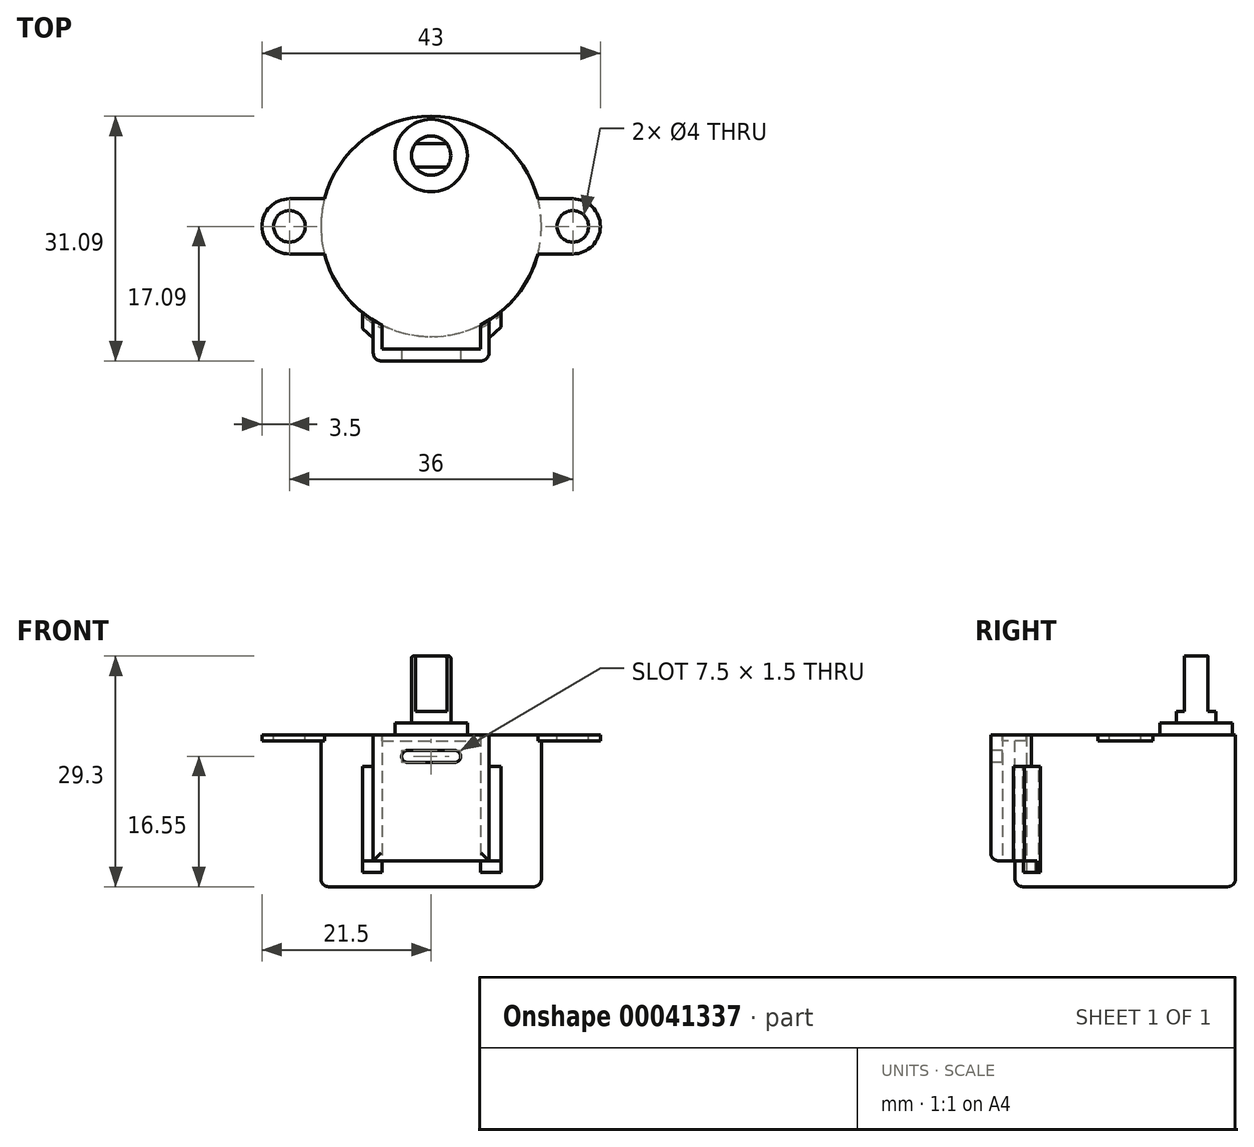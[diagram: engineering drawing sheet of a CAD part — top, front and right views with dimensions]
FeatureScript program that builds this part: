
annotation { "Feature Type Name" : "Feature", "Feature Type Description" : "" }
export const myFeature = defineFeature(function(context is Context, id is Id, definition is map)
    precondition{}
    {
        {
            var Q0;
            Q0=qCreatedBy(makeId("Top.planeOp"),FACE);
            var sketch = newSketch(context, id + "F0", { "sketchPlane" : qUnion([Q0])});
            skCircle(sketch, "E0", {"center": v(0, 0) * mm, "radius": 14 * mm});
            skLineSegment(sketch, "E1", {"start": v(-13.56, 3.5) * mm, "end": v(-18, 3.5) * mm});
            skLineSegment(sketch, "E2", {"start": v(-13.56, -3.5) * mm, "end": v(-18, -3.5) * mm});
            skArc(sketch, "E3", {"start": v(-18, -3.5) * mm, "mid": v(-21.5, 0) * mm, "end": v(-18, 3.5) * mm});
            skCircle(sketch, "E4", {"center": v(-18, 0) * mm, "radius": 2 * mm});
            skLineSegment(sketch, "E5", {"start": v(0, 23.7) * mm, "end": v(0, -18.74) * mm, "construction": true});
            skLineSegment(sketch, "E6.MirrorCS", {"start": v(13.56, -3.5) * mm, "end": v(18, -3.5) * mm});
            skLineSegment(sketch, "E7.MirrorCS", {"start": v(13.56, 3.5) * mm, "end": v(18, 3.5) * mm});
            skArc(sketch, "E8.MirrorCS", {"start": v(18, -3.5) * mm, "mid": v(21.5, 0) * mm, "end": v(18, 3.5) * mm});
            skCircle(sketch, "E9.MirrorC", {"center": v(18, 0) * mm, "radius": 2 * mm});
            skLineSegment(sketch, "E10", {"start": v(-6.25, -12.53) * mm, "end": v(-6.25, -15.6) * mm});
            skLineSegment(sketch, "E11", {"start": v(-6.25, -15.6) * mm, "end": v(6.25, -15.6) * mm});
            skLineSegment(sketch, "E12", {"start": v(6.25, -15.6) * mm, "end": v(6.25, -12.53) * mm});
            skCircle(sketch, "E13", {"center": v(0, 9) * mm, "radius": 4.6 * mm});
            skCircle(sketch, "E14", {"center": v(0, 9) * mm, "radius": 2.5 * mm});
            skLineSegment(sketch, "E15", {"start": v(7.35, -11.92) * mm, "end": v(7.35, -17.1) * mm});
            skLineSegment(sketch, "E16", {"start": v(7.35, -17.1) * mm, "end": v(-7.35, -17.1) * mm});
            skLineSegment(sketch, "E17", {"start": v(-7.35, -17.1) * mm, "end": v(-7.35, -11.92) * mm});
            skLineSegment(sketch, "E18", {"start": v(8.9, -10.8) * mm, "end": v(8.9, -12.8) * mm});
            skLineSegment(sketch, "E19", {"start": v(8.9, -12.8) * mm, "end": v(7.35, -14.21) * mm});
            skLineSegment(sketch, "E20", {"start": v(-8.7, -10.97) * mm, "end": v(-8.7, -12.97) * mm});
            skLineSegment(sketch, "E21", {"start": v(-8.7, -12.97) * mm, "end": v(-7.35, -14.21) * mm});
            skPoint(sketch, "E22", {"position": v(-7.35, -14.5) * mm});
            skArc(sketch, "E23.trimOffspring", {"start": v(-8.7, -11.4) * mm, "mid": v(-5.3, -13.35) * mm, "end": v(-1.5, -14.3) * mm});
            skLineSegment(sketch, "E24", {"start": v(1.5, -14.3) * mm, "end": v(1.5, -13.92) * mm});
            skLineSegment(sketch, "E25", {"start": v(-1.5, -14.3) * mm, "end": v(-1.5, -13.92) * mm});
            skArc(sketch, "E26.trimOffspring", {"start": v(1.5, -14.3) * mm, "mid": v(5.43, -13.3) * mm, "end": v(8.9, -11.22) * mm});
            skLineSegment(sketch, "E27", {"start": v(-2, 10.5) * mm, "end": v(2, 10.5) * mm});
            skLineSegment(sketch, "E28", {"start": v(-2, 7.5) * mm, "end": v(2, 7.5) * mm});
            skSolve(sketch);
        }
        {
            var Q0;
            {var subQ0=sQuery(id+"F0.wireOp",EDGE,"E1");Q0=makeQuery(id+"F0.imprint","IMPRINT",FACE,{"disambiguationData":[TD([[makeQuery(id+"F0.imprint","IMPRINT",EDGE,{"derivedFrom":subQ0}),1.0]])]});}
            var Q1;
            Q1=makeQuery(id+"F0.imprint","IMPRINT",FACE,{"disambiguationData":[TD([[makeQuery(id+"F0.imprint","IMPRINT",EDGE,{"derivedFrom":sQuery(id+"F0.wireOp",EDGE,"E13")}),-1.0]])]});
            var Q2;
            {var subQ0=sQuery(id+"F0.wireOp",EDGE,"E6.MirrorCS");Q2=makeQuery(id+"F0.imprint","IMPRINT",FACE,{"disambiguationData":[TD([[makeQuery(id+"F0.imprint","IMPRINT",EDGE,{"derivedFrom":subQ0}),1.0]])]});}
            var Q3;
            Q3=makeQuery(id+"F0.imprint","IMPRINT",FACE,{"disambiguationData":[TD([[makeQuery(id+"F0.imprint","IMPRINT",EDGE,{"derivedFrom":sQuery(id+"F0.wireOp",EDGE,"E13")}),1.0]])]});
            var Q4;
            Q4=makeQuery(id+"F0.imprint","IMPRINT",FACE,{"disambiguationData":[TD([[makeQuery(id+"F0.imprint","IMPRINT",EDGE,{"derivedFrom":sQuery(id+"F0.wireOp",EDGE,"E14")}),1.0]])]});
            var Q5;
            {var subQ0=sQuery(id+"F0.wireOp",EDGE,"E10");Q5=makeQuery(id+"F0.imprint","IMPRINT",FACE,{"disambiguationData":[TD([[makeQuery(id+"F0.imprint","IMPRINT",EDGE,{"derivedFrom":subQ0}),1.0]])]});}
            var Q6;
            {var subQ9=sQuery(id+"F0.wireOp",EDGE,"E11");Q6=makeQuery(id+"F0.imprint","IMPRINT",FACE,{"disambiguationData":[TD([[makeQuery(id+"F0.imprint","IMPRINT",EDGE,{"derivedFrom":subQ9}),1.0]])]});}
            var Q7;
            {var subQ3=sQuery(id+"F0.wireOp",EDGE,"E24");Q7=makeQuery(id+"F0.imprint","IMPRINT",FACE,{"disambiguationData":[TD([[makeQuery(id+"F0.imprint","IMPRINT",EDGE,{"derivedFrom":subQ3}),-1.0]])]});}
            var Q8;
            {var subQ0=sQuery(id+"F0.wireOp",EDGE,"E27");Q8=makeQuery(id+"F0.imprint","IMPRINT",FACE,{"disambiguationData":[TD([[makeQuery(id+"F0.imprint","IMPRINT",EDGE,{"derivedFrom":subQ0}),1.0]])]});}
            var Q9;
            {var subQ0=sQuery(id+"F0.wireOp",EDGE,"E28");Q9=makeQuery(id+"F0.imprint","IMPRINT",FACE,{"disambiguationData":[TD([[makeQuery(id+"F0.imprint","IMPRINT",EDGE,{"derivedFrom":subQ0}),-1.0]])]});}
            extrude(context, id + "F1", {"entities" : qUnion([Q0, Q1, Q2, Q3, Q4, Q5, Q6, Q7, Q8, Q9]), "oppositeDirection" : true, "depth" : 0.8 * mm});
        }
        {
            var Q0;
            Q0=makeQuery(id+"F0.imprint","IMPRINT",FACE,{"disambiguationData":[TD([[makeQuery(id+"F0.imprint","IMPRINT",EDGE,{"derivedFrom":sQuery(id+"F0.wireOp",EDGE,"E13")}),-1.0]])]});
            var Q1;
            Q1=makeQuery(id+"F0.imprint","IMPRINT",FACE,{"disambiguationData":[TD([[makeQuery(id+"F0.imprint","IMPRINT",EDGE,{"derivedFrom":sQuery(id+"F0.wireOp",EDGE,"E14")}),1.0]])]});
            var Q2;
            Q2=makeQuery(id+"F0.imprint","IMPRINT",FACE,{"disambiguationData":[TD([[makeQuery(id+"F0.imprint","IMPRINT",EDGE,{"derivedFrom":sQuery(id+"F0.wireOp",EDGE,"E13")}),1.0]])]});
            var Q3;
            {var subQ0=sQuery(id+"F0.wireOp",EDGE,"E27");Q3=makeQuery(id+"F0.imprint","IMPRINT",FACE,{"disambiguationData":[TD([[makeQuery(id+"F0.imprint","IMPRINT",EDGE,{"derivedFrom":subQ0}),1.0]])]});}
            var Q4;
            {var subQ0=sQuery(id+"F0.wireOp",EDGE,"E28");Q4=makeQuery(id+"F0.imprint","IMPRINT",FACE,{"disambiguationData":[TD([[makeQuery(id+"F0.imprint","IMPRINT",EDGE,{"derivedFrom":subQ0}),-1.0]])]});}
            extrude(context, id + "F2", {"entities" : qUnion([Q0, Q1, Q2, Q3, Q4]), "operationType" : NewBodyOperationType.ADD, "oppositeDirection" : true, "depth" : 19.3 * mm});
        }
        {
            var Q0;
            Q0=makeQuery(id+"F2.opExtrude","CAP_EDGE",EDGE,{"disambiguationData":[OSD([sQuery(id+"F0.wireOp",EDGE,"E0")])],"isStart":false});
            fillet(context, id + "F3", {"entities" : qUnion([Q0]), "radius" : 1 * mm, "tangentPropagation" : true, "allowEdgeOverflow" : false});
        }
        {
            var Q0;
            Q0=makeQuery(id+"F0.imprint","IMPRINT",FACE,{"disambiguationData":[TD([[makeQuery(id+"F0.imprint","IMPRINT",EDGE,{"derivedFrom":sQuery(id+"F0.wireOp",EDGE,"E13")}),1.0]])]});
            extrude(context, id + "F4", {"entities" : qUnion([Q0]), "operationType" : NewBodyOperationType.ADD, "depth" : 1.5 * mm});
        }
        {
            var Q0;
            Q0=makeQuery(id+"F0.imprint","IMPRINT",FACE,{"disambiguationData":[TD([[makeQuery(id+"F0.imprint","IMPRINT",EDGE,{"derivedFrom":sQuery(id+"F0.wireOp",EDGE,"E13")}),-1.0]])]});
            cPlane(context, id + "F5", {"entities" : qUnion([Q0]), "cplaneType" : CPlaneType.OFFSET, "offset" : 4 * mm, "oppositeDirection" : true, "width" : 150 * mm, "height" : 150 * mm});
        }
        {
            var Q0;
            Q0=qCreatedBy(id+"F5.planeOp",FACE);
            var sketch = newSketch(context, id + "F6", { "sketchPlane" : qUnion([Q0])});
            skCircle(sketch, "E29.0", {"center": v(0, 0) * mm, "radius": 14 * mm});
            skLineSegment(sketch, "E30.0", {"start": v(-8.7, -10.97) * mm, "end": v(-8.7, -12.97) * mm});
            skLineSegment(sketch, "E31.0", {"start": v(-8.7, -12.97) * mm, "end": v(-7.35, -14.21) * mm});
            skLineSegment(sketch, "E32.0.0", {"start": v(-6.25, -15.6) * mm, "end": v(-6.25, -12.93) * mm});
            skArc(sketch, "E32.0.1", {"start": v(-6.25, -12.93) * mm, "mid": v(-6.8, -12.64) * mm, "end": v(-7.35, -12.32) * mm});
            skLineSegment(sketch, "E32.0.2", {"start": v(-7.35, -12.32) * mm, "end": v(-7.35, -14.21) * mm});
            skLineSegment(sketch, "E32.0.3", {"start": v(-7.35, -14.21) * mm, "end": v(-7.35, -17.1) * mm});
            skLineSegment(sketch, "E32.0.4", {"start": v(-7.35, -17.1) * mm, "end": v(7.35, -17.1) * mm});
            skLineSegment(sketch, "E32.0.5", {"start": v(7.35, -17.1) * mm, "end": v(7.35, -14.21) * mm});
            skLineSegment(sketch, "E32.0.6", {"start": v(7.35, -14.21) * mm, "end": v(7.35, -12.32) * mm});
            skArc(sketch, "E32.0.7", {"start": v(7.35, -12.32) * mm, "mid": v(6.8, -12.64) * mm, "end": v(6.25, -12.93) * mm});
            skLineSegment(sketch, "E32.0.8", {"start": v(6.25, -12.93) * mm, "end": v(6.25, -15.6) * mm});
            skLineSegment(sketch, "E32.0.9", {"start": v(6.25, -15.6) * mm, "end": v(-6.25, -15.6) * mm});
            skLineSegment(sketch, "E33.0", {"start": v(8.9, -12.8) * mm, "end": v(7.35, -14.21) * mm});
            skLineSegment(sketch, "E34.0", {"start": v(8.9, -10.8) * mm, "end": v(8.9, -12.8) * mm});
            skArc(sketch, "E35.0", {"start": v(-8.7, -11.4) * mm, "mid": v(-5.3, -13.35) * mm, "end": v(-1.5, -14.3) * mm});
            skArc(sketch, "E36.0", {"start": v(1.5, -14.3) * mm, "mid": v(5.43, -13.3) * mm, "end": v(8.9, -11.22) * mm});
            skArc(sketch, "E37.0.0", {"start": v(-1.5, -14.3) * mm, "mid": v(-3.94, -13.82) * mm, "end": v(-6.25, -12.93) * mm});
            skLineSegment(sketch, "E37.0.1", {"start": v(-6.25, -12.93) * mm, "end": v(-6.25, -15.6) * mm});
            skLineSegment(sketch, "E37.0.2", {"start": v(-6.25, -15.6) * mm, "end": v(6.25, -15.6) * mm});
            skLineSegment(sketch, "E37.0.3", {"start": v(6.25, -15.6) * mm, "end": v(6.25, -12.93) * mm});
            skArc(sketch, "E37.0.4", {"start": v(6.25, -12.93) * mm, "mid": v(3.94, -13.82) * mm, "end": v(1.5, -14.3) * mm});
            skLineSegment(sketch, "E37.0.5", {"start": v(1.5, -14.3) * mm, "end": v(1.5, -13.92) * mm});
            skArc(sketch, "E37.0.6", {"start": v(1.5, -13.92) * mm, "mid": v(0, -14) * mm, "end": v(-1.5, -13.92) * mm});
            skLineSegment(sketch, "E37.0.7", {"start": v(-1.5, -13.92) * mm, "end": v(-1.5, -14.3) * mm});
            skLineSegment(sketch, "E38.0", {"start": v(-7.35, -17.1) * mm, "end": v(-7.35, -11.92) * mm});
            skLineSegment(sketch, "E39.0", {"start": v(-6.25, -12.53) * mm, "end": v(-6.25, -15.6) * mm});
            skLineSegment(sketch, "E40.0", {"start": v(7.35, -11.92) * mm, "end": v(7.35, -17.1) * mm});
            skLineSegment(sketch, "E41.0", {"start": v(6.25, -15.6) * mm, "end": v(6.25, -12.53) * mm});
            skSolve(sketch);
        }
        {
            var Q0;
            {var subQ7=sQuery(id+"F6.wireOp",EDGE,"E32.0.4");Q0=makeQuery(id+"F6.imprint","IMPRINT",FACE,{"disambiguationData":[TD([[makeQuery(id+"F6.imprint","IMPRINT",EDGE,{"derivedFrom":subQ7}),1.0]])]});}
            var Q1;
            {var subQ1=sQuery(id+"F6.wireOp",EDGE,"E29.0");var subQ5=sQuery(id+"F6.wireOp",EDGE,"E38.0");var subQ7=makeQuery(id+"F6.imprint","INTERSECT",VERTEX,{"derivedFrom":[subQ1,subQ5]});Q1=makeQuery(id+"F6.imprint","IMPRINT",FACE,{"disambiguationData":[TD([[makeQuery(id+"F6.imprint","IMPRINT",EDGE,{"disambiguationData":[TD([[subQ7,-1.0]])],"derivedFrom":subQ1}),-1.0]])]});}
            var Q2;
            {var subQ0=sQuery(id+"F6.wireOp",EDGE,"E40.0");var subQ3=sQuery(id+"F6.wireOp",EDGE,"E29.0");var subQ4=makeQuery(id+"F6.imprint","INTERSECT",VERTEX,{"derivedFrom":[subQ3,subQ0]});Q2=makeQuery(id+"F6.imprint","IMPRINT",FACE,{"disambiguationData":[TD([[makeQuery(id+"F6.imprint","IMPRINT",EDGE,{"disambiguationData":[TD([[subQ4,1.0]])],"derivedFrom":subQ3}),-1.0]])]});}
            extrude(context, id + "F7", {"entities" : qUnion([Q0, Q1, Q2]), "depth" : 4 * mm});
        }
        {
            var Q0;
            {var subQ7=sQuery(id+"F6.wireOp",EDGE,"E32.0.4");Q0=makeQuery(id+"F6.imprint","IMPRINT",FACE,{"disambiguationData":[TD([[makeQuery(id+"F6.imprint","IMPRINT",EDGE,{"derivedFrom":subQ7}),1.0]])]});}
            var Q1;
            {var subQ3=sQuery(id+"F6.wireOp",EDGE,"E37.0.0");Q1=makeQuery(id+"F6.imprint","IMPRINT",FACE,{"disambiguationData":[TD([[makeQuery(id+"F6.imprint","IMPRINT",EDGE,{"derivedFrom":subQ3}),-1.0]])]});}
            var Q2;
            {var subQ1=sQuery(id+"F6.wireOp",EDGE,"E29.0");var subQ5=sQuery(id+"F6.wireOp",EDGE,"E38.0");var subQ7=makeQuery(id+"F6.imprint","INTERSECT",VERTEX,{"derivedFrom":[subQ1,subQ5]});Q2=makeQuery(id+"F6.imprint","IMPRINT",FACE,{"disambiguationData":[TD([[makeQuery(id+"F6.imprint","IMPRINT",EDGE,{"disambiguationData":[TD([[subQ7,-1.0]])],"derivedFrom":subQ1}),-1.0]])]});}
            var Q3;
            {var subQ3=sQuery(id+"F6.wireOp",EDGE,"E29.0");var subQ5=sQuery(id+"F6.wireOp",EDGE,"E30.0");var subQ7=makeQuery(id+"F6.imprint","INTERSECT",VERTEX,{"derivedFrom":[subQ3,subQ5]});Q3=makeQuery(id+"F6.imprint","IMPRINT",FACE,{"disambiguationData":[TD([[makeQuery(id+"F6.imprint","IMPRINT",EDGE,{"disambiguationData":[TD([[subQ7,-1.0]])],"derivedFrom":subQ3}),-1.0]])]});}
            var Q4;
            {var subQ3=sQuery(id+"F6.wireOp",EDGE,"E31.0");Q4=makeQuery(id+"F6.imprint","IMPRINT",FACE,{"disambiguationData":[TD([[makeQuery(id+"F6.imprint","IMPRINT",EDGE,{"derivedFrom":subQ3}),1.0]])]});}
            var Q5;
            {var subQ0=sQuery(id+"F6.wireOp",EDGE,"E40.0");var subQ3=sQuery(id+"F6.wireOp",EDGE,"E29.0");var subQ4=makeQuery(id+"F6.imprint","INTERSECT",VERTEX,{"derivedFrom":[subQ3,subQ0]});Q5=makeQuery(id+"F6.imprint","IMPRINT",FACE,{"disambiguationData":[TD([[makeQuery(id+"F6.imprint","IMPRINT",EDGE,{"disambiguationData":[TD([[subQ4,1.0]])],"derivedFrom":subQ3}),-1.0]])]});}
            var Q6;
            {var subQ3=sQuery(id+"F6.wireOp",EDGE,"E29.0");var subQ5=sQuery(id+"F6.wireOp",EDGE,"E34.0");var subQ7=makeQuery(id+"F6.imprint","INTERSECT",VERTEX,{"derivedFrom":[subQ3,subQ5]});Q6=makeQuery(id+"F6.imprint","IMPRINT",FACE,{"disambiguationData":[TD([[makeQuery(id+"F6.imprint","IMPRINT",EDGE,{"disambiguationData":[TD([[subQ7,1.0]])],"derivedFrom":subQ3}),-1.0]])]});}
            var Q7;
            {var subQ3=sQuery(id+"F6.wireOp",EDGE,"E33.0");Q7=makeQuery(id+"F6.imprint","IMPRINT",FACE,{"disambiguationData":[TD([[makeQuery(id+"F6.imprint","IMPRINT",EDGE,{"derivedFrom":subQ3}),-1.0]])]});}
            var Q8;
            {var subQ1=sQuery(id+"F6.wireOp",EDGE,"E37.0.4");Q8=makeQuery(id+"F6.imprint","IMPRINT",FACE,{"disambiguationData":[TD([[makeQuery(id+"F6.imprint","IMPRINT",EDGE,{"derivedFrom":subQ1}),-1.0]])]});}
            var Q9;
            {var subQ6=sQuery(id+"F6.wireOp",EDGE,"E37.0.0");Q9=makeQuery(id+"F6.imprint","IMPRINT",FACE,{"disambiguationData":[TD([[makeQuery(id+"F6.imprint","IMPRINT",EDGE,{"derivedFrom":subQ6}),1.0]])]});}
            extrude(context, id + "F8", {"entities" : qUnion([Q0, Q1, Q2, Q3, Q4, Q5, Q6, Q7, Q8, Q9]), "oppositeDirection" : true, "depth" : 12 * mm});
        }
        {
            var Q0;
            {var subQ3=sQuery(id+"F6.wireOp",EDGE,"E29.0");var subQ5=sQuery(id+"F6.wireOp",EDGE,"E30.0");var subQ7=makeQuery(id+"F6.imprint","INTERSECT",VERTEX,{"derivedFrom":[subQ3,subQ5]});Q0=makeQuery(id+"F6.imprint","IMPRINT",FACE,{"disambiguationData":[TD([[makeQuery(id+"F6.imprint","IMPRINT",EDGE,{"disambiguationData":[TD([[subQ7,-1.0]])],"derivedFrom":subQ3}),-1.0]])]});}
            var Q1;
            {var subQ1=sQuery(id+"F6.wireOp",EDGE,"E29.0");var subQ5=sQuery(id+"F6.wireOp",EDGE,"E38.0");var subQ7=makeQuery(id+"F6.imprint","INTERSECT",VERTEX,{"derivedFrom":[subQ1,subQ5]});Q1=makeQuery(id+"F6.imprint","IMPRINT",FACE,{"disambiguationData":[TD([[makeQuery(id+"F6.imprint","IMPRINT",EDGE,{"disambiguationData":[TD([[subQ7,-1.0]])],"derivedFrom":subQ1}),-1.0]])]});}
            var Q2;
            {var subQ3=sQuery(id+"F6.wireOp",EDGE,"E37.0.0");Q2=makeQuery(id+"F6.imprint","IMPRINT",FACE,{"disambiguationData":[TD([[makeQuery(id+"F6.imprint","IMPRINT",EDGE,{"derivedFrom":subQ3}),-1.0]])]});}
            var Q3;
            {var subQ1=sQuery(id+"F6.wireOp",EDGE,"E37.0.4");Q3=makeQuery(id+"F6.imprint","IMPRINT",FACE,{"disambiguationData":[TD([[makeQuery(id+"F6.imprint","IMPRINT",EDGE,{"derivedFrom":subQ1}),-1.0]])]});}
            var Q4;
            {var subQ0=sQuery(id+"F6.wireOp",EDGE,"E40.0");var subQ3=sQuery(id+"F6.wireOp",EDGE,"E29.0");var subQ4=makeQuery(id+"F6.imprint","INTERSECT",VERTEX,{"derivedFrom":[subQ3,subQ0]});Q4=makeQuery(id+"F6.imprint","IMPRINT",FACE,{"disambiguationData":[TD([[makeQuery(id+"F6.imprint","IMPRINT",EDGE,{"disambiguationData":[TD([[subQ4,1.0]])],"derivedFrom":subQ3}),-1.0]])]});}
            var Q5;
            {var subQ3=sQuery(id+"F6.wireOp",EDGE,"E29.0");var subQ5=sQuery(id+"F6.wireOp",EDGE,"E34.0");var subQ7=makeQuery(id+"F6.imprint","INTERSECT",VERTEX,{"derivedFrom":[subQ3,subQ5]});Q5=makeQuery(id+"F6.imprint","IMPRINT",FACE,{"disambiguationData":[TD([[makeQuery(id+"F6.imprint","IMPRINT",EDGE,{"disambiguationData":[TD([[subQ7,1.0]])],"derivedFrom":subQ3}),-1.0]])]});}
            extrude(context, id + "F9", {"entities" : qUnion([Q0, Q1, Q2, Q3, Q4, Q5]), "oppositeDirection" : true, "depth" : 13.5 * mm});
        }
        {
            var Q0;
            Q0=makeQuery(id+"F7.opExtrude","SWEPT_BODY",BODY,{"disambiguationData":[OSD([sQuery(id+"F6.wireOp",EDGE,"E29.0"),sQuery(id+"F6.wireOp",EDGE,"E32.0.4"),sQuery(id+"F6.wireOp",EDGE,"E37.0.2"),sQuery(id+"F6.wireOp",EDGE,"E38.0"),sQuery(id+"F6.wireOp",EDGE,"E39.0"),sQuery(id+"F6.wireOp",EDGE,"E40.0"),sQuery(id+"F6.wireOp",EDGE,"E41.0")])]});
            var Q1;
            Q1=makeQuery(id+"F8.opExtrude","SWEPT_BODY",BODY,{"disambiguationData":[OSD([sQuery(id+"F6.wireOp",EDGE,"E29.0"),sQuery(id+"F6.wireOp",EDGE,"E30.0"),sQuery(id+"F6.wireOp",EDGE,"E31.0"),sQuery(id+"F6.wireOp",EDGE,"E32.0.4"),sQuery(id+"F6.wireOp",EDGE,"E33.0"),sQuery(id+"F6.wireOp",EDGE,"E34.0"),sQuery(id+"F6.wireOp",EDGE,"E38.0"),sQuery(id+"F6.wireOp",EDGE,"E40.0")])]});
            var Q2;
            Q2=makeQuery(id+"F9.opExtrude","SWEPT_BODY",BODY,{"disambiguationData":[OSD([sQuery(id+"F6.wireOp",EDGE,"E29.0"),sQuery(id+"F6.wireOp",EDGE,"E30.0"),sQuery(id+"F6.wireOp",EDGE,"E35.0"),sQuery(id+"F6.wireOp",EDGE,"E37.0.0"),sQuery(id+"F6.wireOp",EDGE,"E37.0.7")])]});
            var Q3;
            Q3=makeQuery(id+"F9.opExtrude","SWEPT_BODY",BODY,{"disambiguationData":[OSD([sQuery(id+"F6.wireOp",EDGE,"E29.0"),sQuery(id+"F6.wireOp",EDGE,"E34.0"),sQuery(id+"F6.wireOp",EDGE,"E36.0"),sQuery(id+"F6.wireOp",EDGE,"E37.0.4"),sQuery(id+"F6.wireOp",EDGE,"E37.0.5")])]});
            booleanBodies(context, id + "F10", {"operationType" : BooleanOperationType.UNION, "tools" : qUnion([Q0, Q1, Q2, Q3])});
        }
        {
            var Q0;
            {var subQ0=sQuery(id+"F6.wireOp",EDGE,"E32.0.4");var subQ1=sQuery(id+"F6.wireOp",EDGE,"E38.0");Q0=makeQuery(id+"F10.opBoolean","MERGE",EDGE,{"derivedFrom":[makeQuery(id+"F7.opExtrude","SWEPT_EDGE",EDGE,{"disambiguationData":[OSD([subQ0,subQ1])]}),makeQuery(id+"F8.opExtrude","SWEPT_EDGE",EDGE,{"disambiguationData":[OSD([subQ0,subQ1])]})]});}
            var Q1;
            Q1=makeQuery(id+"F8.opExtrude","CAP_EDGE",EDGE,{"disambiguationData":[OSD([sQuery(id+"F6.wireOp",EDGE,"E32.0.4")])],"isStart":false});
            var Q2;
            {var subQ0=sQuery(id+"F6.wireOp",EDGE,"E32.0.4");var subQ1=sQuery(id+"F6.wireOp",EDGE,"E40.0");Q2=makeQuery(id+"F10.opBoolean","MERGE",EDGE,{"derivedFrom":[makeQuery(id+"F7.opExtrude","SWEPT_EDGE",EDGE,{"disambiguationData":[OSD([subQ0,subQ1])]}),makeQuery(id+"F8.opExtrude","SWEPT_EDGE",EDGE,{"disambiguationData":[OSD([subQ0,subQ1])]})]});}
            var Q3;
            Q3=makeQuery(id+"F8.opExtrude","CAP_EDGE",EDGE,{"disambiguationData":[OSD([sQuery(id+"F6.wireOp",EDGE,"E38.0")])],"isStart":false});
            var Q4;
            Q4=makeQuery(id+"F8.opExtrude","CAP_EDGE",EDGE,{"disambiguationData":[OSD([sQuery(id+"F6.wireOp",EDGE,"E40.0")])],"isStart":false});
            fillet(context, id + "F11", {"entities" : qUnion([Q0, Q1, Q2, Q3, Q4]), "radius" : 1 * mm, "tangentPropagation" : true, "allowEdgeOverflow" : false});
        }
        {
            var Q0;
            {var subQ0=sQuery(id+"F6.wireOp",EDGE,"E32.0.4");Q0=makeQuery(id+"F10.opBoolean","MERGE",FACE,{"derivedFrom":[makeQuery(id+"F7.opExtrude","SWEPT_FACE",FACE,{"disambiguationData":[OSD([subQ0])]}),makeQuery(id+"F8.opExtrude","SWEPT_FACE",FACE,{"disambiguationData":[OSD([subQ0])]})]});}
            cPlane(context, id + "F12", {"entities" : qUnion([Q0]), "cplaneType" : CPlaneType.OFFSET, "offset" : 0 * mm, "width" : 150 * mm, "height" : 150 * mm});
        }
        {
            var Q0;
            Q0=qCreatedBy(id+"F12.planeOp",FACE);
            var sketch = newSketch(context, id + "F13", { "sketchPlane" : qUnion([Q0])});
            skLineSegment(sketch, "E42.0.0", {"start": v(6.35, 0) * mm, "end": v(-6.35, 0) * mm});
            skLineSegment(sketch, "E42.0.1", {"start": v(-6.35, 0) * mm, "end": v(-6.35, -15) * mm});
            skLineSegment(sketch, "E42.0.2", {"start": v(-6.35, -15) * mm, "end": v(6.35, -15) * mm});
            skLineSegment(sketch, "E42.0.3", {"start": v(6.35, -15) * mm, "end": v(6.35, 0) * mm});
            skLineSegment(sketch, "E43", {"start": v(3, -2) * mm, "end": v(-3, -2) * mm});
            skLineSegment(sketch, "E44", {"start": v(3, -3.5) * mm, "end": v(-3, -3.5) * mm});
            skArc(sketch, "E45", {"start": v(3, -2) * mm, "mid": v(3.75, -2.75) * mm, "end": v(3, -3.5) * mm});
            skArc(sketch, "E46", {"start": v(-3, -3.5) * mm, "mid": v(-3.75, -2.75) * mm, "end": v(-3, -2) * mm});
            skSolve(sketch);
        }
        {
            var Q0;
            Q0=makeQuery(id+"F13.imprint","IMPRINT",FACE,{"disambiguationData":[TD([[makeQuery(id+"F13.imprint","IMPRINT",EDGE,{"derivedFrom":sQuery(id+"F13.wireOp",EDGE,"E43")}),1.0]])]});
            extrude(context, id + "F14", {"entities" : qUnion([Q0]), "operationType" : NewBodyOperationType.REMOVE, "oppositeDirection" : true, "depth" : 3 * mm});
        }
        {
            var Q0;
            {var subQ0=sQuery(id+"F0.wireOp",EDGE,"E27");Q0=makeQuery(id+"F0.imprint","IMPRINT",FACE,{"disambiguationData":[TD([[makeQuery(id+"F0.imprint","IMPRINT",EDGE,{"derivedFrom":subQ0}),1.0]])]});}
            var Q1;
            {var subQ1=sQuery(id+"F0.wireOp",EDGE,"E27");Q1=makeQuery(id+"F0.imprint","IMPRINT",FACE,{"disambiguationData":[TD([[makeQuery(id+"F0.imprint","IMPRINT",EDGE,{"derivedFrom":subQ1}),-1.0]])]});}
            var Q2;
            {var subQ0=sQuery(id+"F0.wireOp",EDGE,"E28");Q2=makeQuery(id+"F0.imprint","IMPRINT",FACE,{"disambiguationData":[TD([[makeQuery(id+"F0.imprint","IMPRINT",EDGE,{"derivedFrom":subQ0}),-1.0]])]});}
            extrude(context, id + "F15", {"entities" : qUnion([Q0, Q1, Q2]), "depth" : 3 * mm});
        }
        {
            var Q0;
            {var subQ1=sQuery(id+"F0.wireOp",EDGE,"E27");Q0=makeQuery(id+"F0.imprint","IMPRINT",FACE,{"disambiguationData":[TD([[makeQuery(id+"F0.imprint","IMPRINT",EDGE,{"derivedFrom":subQ1}),-1.0]])]});}
            extrude(context, id + "F16", {"entities" : qUnion([Q0]), "operationType" : NewBodyOperationType.ADD, "depth" : 10 * mm});
        }
        {
            var Q0;
            {var subQ0=sQuery(id+"F0.wireOp",EDGE,"E14");Q0=makeQuery(id+"F16.opExtrude","CAP_EDGE",EDGE,{"disambiguationData":[OSD([subQ0]),TDD([makeQuery(id+"F0.imprint","IMPRINT",EDGE,{"disambiguationData":[TD([[makeQuery(id+"F0.imprint","INTERSECT",VERTEX,{"disambiguationData":[OD(0.0)],"derivedFrom":[subQ0,sQuery(id+"F0.wireOp",EDGE,"E27")]}),-1.0]])],"derivedFrom":subQ0})])],"isStart":false});}
            var Q1;
            {var subQ0=sQuery(id+"F0.wireOp",EDGE,"E14");Q1=makeQuery(id+"F16.opExtrude","CAP_EDGE",EDGE,{"disambiguationData":[OSD([subQ0]),TDD([makeQuery(id+"F0.imprint","IMPRINT",EDGE,{"disambiguationData":[TD([[makeQuery(id+"F0.imprint","INTERSECT",VERTEX,{"disambiguationData":[OD(1.0)],"derivedFrom":[subQ0,sQuery(id+"F0.wireOp",EDGE,"E27")]}),1.0]])],"derivedFrom":subQ0})])],"isStart":false});}
            fillet(context, id + "F17", {"entities" : qUnion([Q0, Q1]), "radius" : 0.25 * mm, "tangentPropagation" : true, "allowEdgeOverflow" : false});
        }
    });
